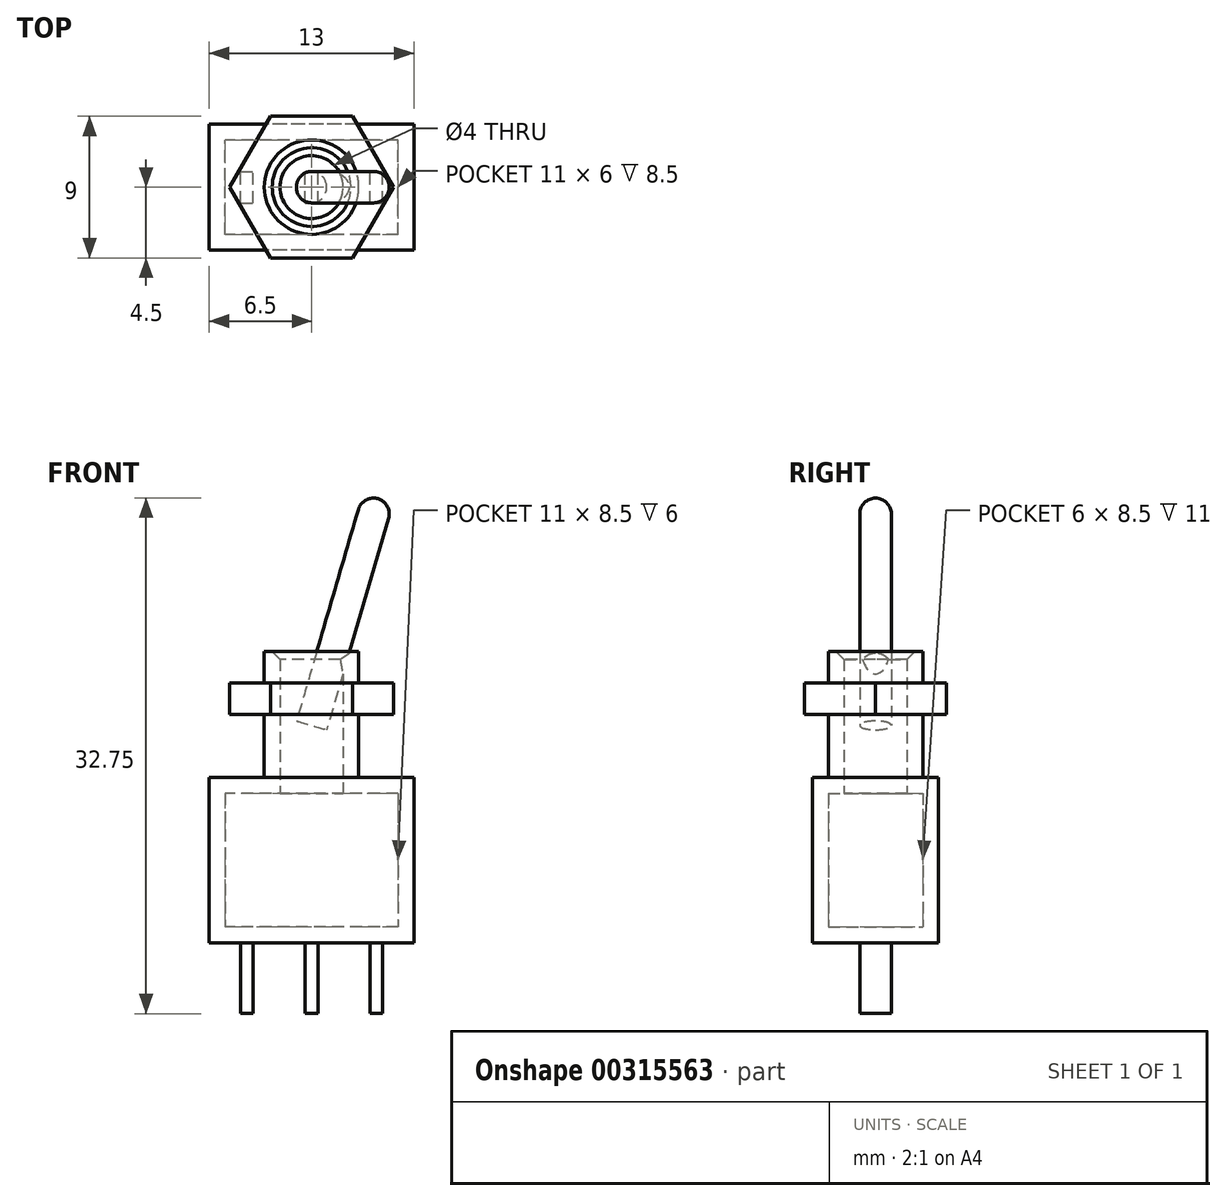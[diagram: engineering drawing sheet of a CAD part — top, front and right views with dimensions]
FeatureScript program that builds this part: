
annotation { "Feature Type Name" : "Feature", "Feature Type Description" : "" }
export const myFeature = defineFeature(function(context is Context, id is Id, definition is map)
    precondition{}
    {
        {
            var Q0;
            Q0=qCreatedBy(makeId("Front.planeOp"),FACE);
            var sketch = newSketch(context, id + "F0", { "sketchPlane" : qUnion([Q0])});
            skLineSegment(sketch, "E0.bottom", {"start": v(6.5, -3.3) * mm, "end": v(-6.5, -3.3) * mm});
            skLineSegment(sketch, "E0.top", {"start": v(6.5, -13.8) * mm, "end": v(4.5, -13.8) * mm});
            skLineSegment(sketch, "E0.left", {"start": v(6.5, -3.3) * mm, "end": v(6.5, -13.8) * mm});
            skLineSegment(sketch, "E0.right", {"start": v(-6.5, -3.3) * mm, "end": v(-6.5, -13.8) * mm});
            skPoint(sketch, "E0.middle", {"position": v(0, -8.56) * mm});
            skLineSegment(sketch, "E1", {"start": v(0, 10) * mm, "end": v(0, -8.56) * mm, "construction": true});
            skLineSegment(sketch, "E2.top", {"start": v(-4.5, -18.3) * mm, "end": v(-3.7, -18.3) * mm});
            skLineSegment(sketch, "E2.left", {"start": v(-4.5, -13.8) * mm, "end": v(-4.5, -18.3) * mm});
            skLineSegment(sketch, "E2.right", {"start": v(-3.7, -13.8) * mm, "end": v(-3.7, -18.3) * mm});
            skLineSegment(sketch, "E3.top", {"start": v(-0.4, -18.3) * mm, "end": v(0.4, -18.3) * mm});
            skLineSegment(sketch, "E3.left", {"start": v(-0.4, -13.8) * mm, "end": v(-0.4, -18.3) * mm});
            skLineSegment(sketch, "E3.right", {"start": v(0.4, -13.8) * mm, "end": v(0.4, -18.3) * mm});
            skLineSegment(sketch, "E4.trimOffspring", {"start": v(-4.5, -13.8) * mm, "end": v(-6.5, -13.8) * mm});
            skLineSegment(sketch, "E5.trimOffspring", {"start": v(-0.4, -13.8) * mm, "end": v(-3.7, -13.8) * mm});
            skLineSegment(sketch, "E6.MirrorCS", {"start": v(3.7, -13.8) * mm, "end": v(3.7, -18.3) * mm});
            skLineSegment(sketch, "E7.MirrorCS", {"start": v(4.5, -18.3) * mm, "end": v(3.7, -18.3) * mm});
            skLineSegment(sketch, "E8.MirrorCS", {"start": v(4.5, -13.8) * mm, "end": v(4.5, -18.3) * mm});
            skLineSegment(sketch, "E9.trimOffspring", {"start": v(3.7, -13.8) * mm, "end": v(0.4, -13.8) * mm});
            skSolve(sketch);
        }
        {
            var Q0;
            Q0 = qSketchRegion(id + "F0", true);
            extrude(context, id + "F1", {"entities" : qUnion([Q0]), "depth" : 8 * mm, "symmetric" : true});
        }
        {
            var Q0;
            Q0=makeQuery(id+"F1.opExtrude","SWEPT_FACE",FACE,{"disambiguationData":[OSD([sQuery(id+"F0.wireOp",EDGE,"E0.left")])]});
            var sketch = newSketch(context, id + "F2", { "sketchPlane" : qUnion([Q0])});
            skLineSegment(sketch, "E10.bottom", {"start": v(-4, -13.8) * mm, "end": v(-1, -13.8) * mm});
            skLineSegment(sketch, "E10.top", {"start": v(-4, -18.3) * mm, "end": v(-1, -18.3) * mm});
            skLineSegment(sketch, "E10.left", {"start": v(-4, -13.8) * mm, "end": v(-4, -18.3) * mm});
            skLineSegment(sketch, "E10.right", {"start": v(-1, -13.8) * mm, "end": v(-1, -18.3) * mm});
            skLineSegment(sketch, "E11.bottom", {"start": v(4, -13.8) * mm, "end": v(1, -13.8) * mm});
            skLineSegment(sketch, "E11.top", {"start": v(4, -18.3) * mm, "end": v(1, -18.3) * mm});
            skLineSegment(sketch, "E11.left", {"start": v(4, -13.8) * mm, "end": v(4, -18.3) * mm});
            skLineSegment(sketch, "E11.right", {"start": v(1, -13.8) * mm, "end": v(1, -18.3) * mm});
            skLineSegment(sketch, "E12", {"start": v(0, -3.3) * mm, "end": v(0, -13.8) * mm, "construction": true});
            skSolve(sketch);
        }
        {
            var Q0;
            Q0 = qSketchRegion(id + "F2", true);
            extrude(context, id + "F3", {"entities" : qUnion([Q0]), "operationType" : NewBodyOperationType.REMOVE, "endBound" : BoundingType.THROUGH_ALL, "oppositeDirection" : true, "depth" : 25 * mm});
        }
        {
            var Q0;
            Q0=makeQuery(id+"F1.opExtrude","SWEPT_FACE",FACE,{"disambiguationData":[OSD([sQuery(id+"F0.wireOp",EDGE,"E0.bottom")])]});
            var sketch = newSketch(context, id + "F4", { "sketchPlane" : qUnion([Q0])});
            skCircle(sketch, "E13", {"center": v(0, 0) * mm, "radius": 3 * mm});
            skSolve(sketch);
        }
        {
            var Q0;
            Q0 = qSketchRegion(id + "F4", true);
            extrude(context, id + "F5", {"entities" : qUnion([Q0]), "operationType" : NewBodyOperationType.ADD, "depth" : 8 * mm});
        }
        {
            var Q0;
            Q0=makeQuery(id+"F1.opExtrude","SWEPT_FACE",FACE,{"disambiguationData":[OSD([sQuery(id+"F0.wireOp",EDGE,"E0.bottom")])]});
            cPlane(context, id + "F6", {"entities" : qUnion([Q0]), "cplaneType" : CPlaneType.OFFSET, "offset" : 4 * mm, "width" : 150 * mm, "height" : 150 * mm});
        }
        {
            var Q0;
            Q0=qCreatedBy(id+"F6.planeOp",FACE);
            var sketch = newSketch(context, id + "F7", { "sketchPlane" : qUnion([Q0])});
            skCircle(sketch, "E14.cCircle", {"center": v(0, 0) * mm, "radius": 4.5 * mm, "construction": true});
            skLineSegment(sketch, "E14.0", {"start": v(5.2, 0) * mm, "end": v(2.6, -4.5) * mm});
            skLineSegment(sketch, "E14.1", {"start": v(2.6, -4.5) * mm, "end": v(-2.6, -4.5) * mm});
            skLineSegment(sketch, "E14.2", {"start": v(-2.6, -4.5) * mm, "end": v(-5.2, 0) * mm});
            skLineSegment(sketch, "E14.3", {"start": v(-5.2, 0) * mm, "end": v(-2.6, 4.5) * mm});
            skLineSegment(sketch, "E14.4", {"start": v(-2.6, 4.5) * mm, "end": v(2.6, 4.5) * mm});
            skLineSegment(sketch, "E14.5", {"start": v(2.6, 4.5) * mm, "end": v(5.2, 0) * mm});
            skPoint(sketch, "E14.0.midPoint", {"position": v(3.9, -2.25) * mm});
            skSolve(sketch);
        }
        {
            var Q0;
            Q0 = qSketchRegion(id + "F7", true);
            extrude(context, id + "F8", {"entities" : qUnion([Q0]), "operationType" : NewBodyOperationType.ADD, "depth" : 2 * mm});
        }
        {
            var Q0;
            Q0=makeQuery(id+"F5.opExtrude","CAP_FACE",FACE,{"disambiguationData":[OSD([sQuery(id+"F4.wireOp",EDGE,"E13")])],"isStart":false});
            shell(context, id + "F9", {"entities" : qUnion([Q0]), "thickness" : 1 * mm});
        }
        {
            var Q0;
            Q0=qCreatedBy(makeId("Front.planeOp"),FACE);
            var sketch = newSketch(context, id + "F10", { "sketchPlane" : qUnion([Q0])});
            skLineSegment(sketch, "E15", {"start": v(0, 0) * mm, "end": v(4.14, 14.16) * mm});
            skSolve(sketch);
        }
        {
            var Q0;
            {var subQ0=sQuery(id+"F4.wireOp",EDGE,"E13");Q0=makeQuery(id+"F9.opShell","OFFSET_EDGE",EDGE,{"disambiguationData":[OSD([subQ0]),TDD([makeQuery(id+"F5.opExtrude","CAP_EDGE",EDGE,{"disambiguationData":[OSD([subQ0])],"isStart":false})])]});}
            chamfer(context, id + "F11", {"entities" : qUnion([Q0]), "width" : 0.5 * mm, "tangentPropagation" : true});
        }
        {
            var Q0;
            Q0=sQuery(id+"F10.wireOp",VERTEX,"E15.start");
            var Q1;
            Q1=sQuery(id+"F10.wireOp",EDGE,"E15");
            cPlane(context, id + "F12", {"entities" : qUnion([Q0, Q1]), "cplaneType" : CPlaneType.LINE_POINT, "offset" : 25 * mm, "width" : 150 * mm, "height" : 150 * mm});
        }
        {
            var Q0;
            Q0=qCreatedBy(id+"F12.planeOp",FACE);
            var sketch = newSketch(context, id + "F13", { "sketchPlane" : qUnion([Q0])});
            skCircle(sketch, "E16", {"center": v(0, 0) * mm, "radius": 1 * mm});
            skSolve(sketch);
        }
        {
            var Q0;
            Q0 = qSketchRegion(id + "F13", true);
            extrude(context, id + "F14", {"entities" : qUnion([Q0]), "operationType" : NewBodyOperationType.ADD, "depth" : 15 * mm});
        }
        {
            var Q0;
            Q0=makeQuery(id+"F14.opExtrude","CAP_EDGE",EDGE,{"disambiguationData":[OSD([sQuery(id+"F13.wireOp",EDGE,"E16")])],"isStart":false});
            fillet(context, id + "F15", {"entities" : qUnion([Q0]), "radius" : 1 * mm, "tangentPropagation" : true, "allowEdgeOverflow" : false});
        }
    });
